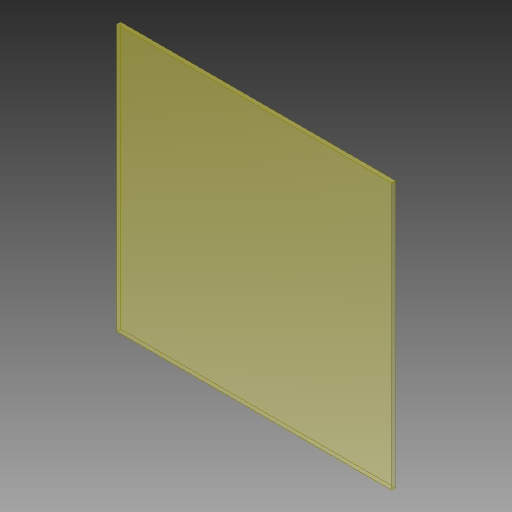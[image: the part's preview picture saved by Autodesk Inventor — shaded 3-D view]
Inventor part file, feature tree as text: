
AUTODESK INVENTOR PART (.ipt)
format: ipt  version: 2019 (Build 230136000, 136)  size: 93,696 bytes
history: native  units: in
note: dims shown in document units (in); Inventor stores cm internally (conversion verified against a paired STEP export)
features: other x1, extrude x1, sketch x1
ambient origin geometry x8: Origin, YZ Plane, XZ Plane, XY Plane, X Axis, Y Axis, Z Axis, Center Point
bodies: Solid1 (feature_tree)
feature tree (3):
  other  "theplate"
  extrude  "Extrusion1"  Depth=8.5in
  sketch  "Sketch1"  dims[d0=8.787in d1=8.5in d2=0.125in d3=0.0in]
